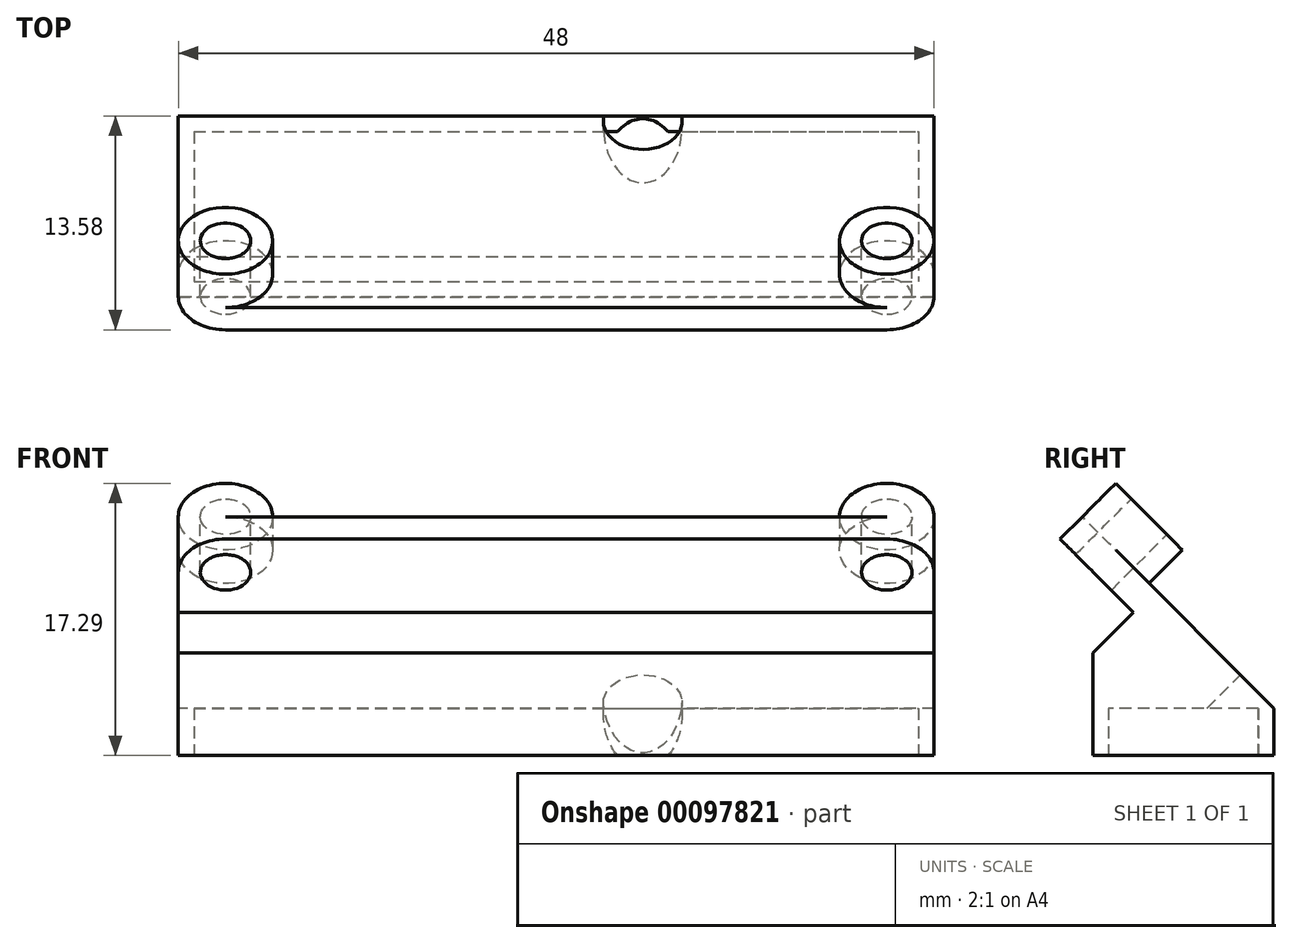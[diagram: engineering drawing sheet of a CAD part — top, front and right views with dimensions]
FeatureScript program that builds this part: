
annotation { "Feature Type Name" : "Feature", "Feature Type Description" : "" }
export const myFeature = defineFeature(function(context is Context, id is Id, definition is map)
    precondition{}
    {
        {
            var Q0;
            Q0=qCreatedBy(makeId("Top.planeOp"),FACE);
            var sketch = newSketch(context, id + "F0", { "sketchPlane" : qUnion([Q0])});
            skLineSegment(sketch, "E0.bottom", {"start": v(-19.1, 2.02) * mm, "end": v(28.9, 2.02) * mm});
            skLineSegment(sketch, "E0.top", {"start": v(-19.1, -9.48) * mm, "end": v(28.9, -9.48) * mm});
            skLineSegment(sketch, "E0.left", {"start": v(-19.1, 2.02) * mm, "end": v(-19.1, -9.48) * mm});
            skLineSegment(sketch, "E0.right", {"start": v(28.9, 2.02) * mm, "end": v(28.9, -9.48) * mm});
            skSolve(sketch);
        }
        {
            var Q0;
            Q0 = qSketchRegion(id + "F0", true);
            var Q1;
            Q1 = qSketchRegion(id + "F2", true);
            extrude(context, id + "F1", {"entities" : qUnion([Q0, Q1]), "depth" : 20 * mm});
        }
        {
            var Q0;
            Q0=qCreatedBy(makeId("Top.planeOp"),FACE);
            var sketch = newSketch(context, id + "F2", { "sketchPlane" : qUnion([Q0])});
            skLineSegment(sketch, "E1.bottom", {"start": v(-18.1, 1.02) * mm, "end": v(27.9, 1.02) * mm});
            skLineSegment(sketch, "E1.top", {"start": v(-18.1, -8.48) * mm, "end": v(27.9, -8.48) * mm});
            skLineSegment(sketch, "E1.left", {"start": v(-18.1, 1.02) * mm, "end": v(-18.1, -8.48) * mm});
            skLineSegment(sketch, "E1.right", {"start": v(27.9, 1.02) * mm, "end": v(27.9, -8.48) * mm});
            skSolve(sketch);
        }
        {
            var Q0;
            Q0 = qSketchRegion(id + "F2", true);
            extrude(context, id + "F3", {"entities" : qUnion([Q0]), "operationType" : NewBodyOperationType.REMOVE, "depth" : 3 * mm});
        }
        {
            var Q0;
            Q0=qCreatedBy(makeId("Right.planeOp"),FACE);
            var sketch = newSketch(context, id + "F4", { "sketchPlane" : qUnion([Q0])});
            skLineSegment(sketch, "E2", {"start": v(2.02, 3) * mm, "end": v(-5.48, 10.5) * mm});
            skLineSegment(sketch, "E3", {"start": v(-5.48, 10.5) * mm, "end": v(-12.98, 3) * mm});
            skLineSegment(sketch, "E4", {"start": v(-12.98, 3) * mm, "end": v(-12.98, 33) * mm});
            skLineSegment(sketch, "E5", {"start": v(-12.98, 33) * mm, "end": v(2.02, 33) * mm});
            skLineSegment(sketch, "E6", {"start": v(2.02, 33) * mm, "end": v(2.02, 3) * mm});
            skSolve(sketch);
        }
        {
            var Q0;
            Q0 = qSketchRegion(id + "F4", true);
            extrude(context, id + "F5", {"entities" : qUnion([Q0]), "operationType" : NewBodyOperationType.REMOVE, "depth" : 40 * mm, "hasSecondDirection" : true, "secondDirectionOppositeDirection" : true, "secondDirectionDepth" : 40 * mm});
        }
        {
            var Q0;
            Q0=makeQuery(id+"F5.boolean.opBoolean","COPY",FACE,{"derivedFrom":makeQuery(id+"F5.opExtrude","SWEPT_FACE",FACE,{"disambiguationData":[OSD([sQuery(id+"F4.wireOp",EDGE,"E2")])]})});
            var sketch = newSketch(context, id + "F6", { "sketchPlane" : qUnion([Q0])});
            skPoint(sketch, "E7", {"position": v(-10.4, 1.2) * mm});
            skSolve(sketch);
        }
        {
            var Q0;
            Q0=sQuery(id+"F6.wireOp",VERTEX,"E7");
            var Q1;
            Q1=makeQuery(id+"F1.opExtrude","SWEPT_BODY",BODY,{"disambiguationData":[OSD([sQuery(id+"F0.wireOp",EDGE,"E0.bottom"),sQuery(id+"F0.wireOp",EDGE,"E0.top"),sQuery(id+"F0.wireOp",EDGE,"E0.left"),sQuery(id+"F0.wireOp",EDGE,"E0.right")])]});
            hole(context, id + "F7", {"style" : HoleStyle.SIMPLE, "endStyle" : HoleEndStyle.BLIND, "holeDiameter" : 5 * mm, "holeDepth" : 10 * mm, "locations" : qUnion([Q0]), "scope" : qUnion([Q1])});
        }
        {
            var Q0;
            Q0=makeQuery(id+"F5.boolean.opBoolean","COPY",FACE,{"derivedFrom":makeQuery(id+"F5.opExtrude","SWEPT_FACE",FACE,{"disambiguationData":[OSD([sQuery(id+"F4.wireOp",EDGE,"E2")])]})});
            cPlane(context, id + "F8", {"entities" : qUnion([Q0]), "cplaneType" : CPlaneType.OFFSET, "offset" : 0 * mm, "width" : 150 * mm, "height" : 150 * mm});
        }
        {
            var Q0;
            Q0=qCreatedBy(id+"F8.planeOp",FACE);
            var sketch = newSketch(context, id + "F9", { "sketchPlane" : qUnion([Q0])});
            skLineSegment(sketch, "E8.bottom", {"start": v(19.1, 8.3) * mm, "end": v(-28.9, 8.3) * mm});
            skLineSegment(sketch, "E8.top", {"start": v(19.1, 17.9) * mm, "end": v(-28.9, 17.9) * mm});
            skLineSegment(sketch, "E8.left", {"start": v(19.1, 8.3) * mm, "end": v(19.1, 17.9) * mm});
            skLineSegment(sketch, "E8.right", {"start": v(-28.9, 8.3) * mm, "end": v(-28.9, 17.9) * mm});
            skPoint(sketch, "E9", {"position": v(16.1, 14.9) * mm});
            skPoint(sketch, "E10", {"position": v(-25.9, 14.9) * mm});
            skSolve(sketch);
        }
        {
            var Q0;
            Q0 = qSketchRegion(id + "F9", true);
            extrude(context, id + "F10", {"entities" : qUnion([Q0]), "operationType" : NewBodyOperationType.ADD, "oppositeDirection" : true, "depth" : 2 * mm});
        }
        {
            var Q0;
            Q0=qCreatedBy(id+"F8.planeOp",FACE);
            var sketch = newSketch(context, id + "F11", { "sketchPlane" : qUnion([Q0])});
            skCircle(sketch, "E11", {"center": v(16.1, 14.9) * mm, "radius": 3 * mm});
            skCircle(sketch, "E12", {"center": v(-25.9, 14.9) * mm, "radius": 3 * mm});
            skSolve(sketch);
        }
        {
            var Q0;
            Q0 = qSketchRegion(id + "F11", true);
            extrude(context, id + "F12", {"entities" : qUnion([Q0]), "operationType" : NewBodyOperationType.ADD, "depth" : 3 * mm});
        }
        {
            var Q0;
            Q0=qCreatedBy(id+"F8.planeOp",FACE);
            var sketch = newSketch(context, id + "F13", { "sketchPlane" : qUnion([Q0])});
            skCircle(sketch, "E13", {"center": v(16.1, 14.9) * mm, "radius": 1.6 * mm});
            skCircle(sketch, "E14", {"center": v(-25.9, 14.9) * mm, "radius": 1.6 * mm});
            skSolve(sketch);
        }
        {
            var Q0;
            Q0 = qSketchRegion(id + "F13", true);
            extrude(context, id + "F14", {"entities" : qUnion([Q0]), "operationType" : NewBodyOperationType.REMOVE, "endBound" : BoundingType.SYMMETRIC, "oppositeDirection" : true, "depth" : 25 * mm});
        }
        {
            var Q0;
            Q0=makeQuery(id+"F10.opExtrude","SWEPT_EDGE",EDGE,{"disambiguationData":[OSD([sQuery(id+"F9.wireOp",EDGE,"E8.top"),sQuery(id+"F9.wireOp",EDGE,"E8.left")])]});
            var Q1;
            Q1=makeQuery(id+"F10.opExtrude","SWEPT_EDGE",EDGE,{"disambiguationData":[OSD([sQuery(id+"F9.wireOp",EDGE,"E8.top"),sQuery(id+"F9.wireOp",EDGE,"E8.right")])]});
            fillet(context, id + "F15", {"entities" : qUnion([Q0, Q1]), "radius" : 3 * mm, "tangentPropagation" : true, "allowEdgeOverflow" : false});
        }
    });
